FCSTD DOCUMENT  (FreeCAD 0.19R)
Label: case
License: All rights reserved
LicenseURL: http://en.wikipedia.org/wiki/All_rights_reserved
objects: Part::FeaturePython×117, Part::Cylinder×32, Part::Box×18, Part::Mirroring×3
note: 170 computed .brp shape members not serialized (recipe doc carries the construction recipe); baked Part::Feature solids carry a one-line shape summary decoded from their .brp

FEATURE [Part::Box] Box002  label="Cube002"
  AttacherType = Attacher::AttachEngine3D
  Height = 10
  Length = 5
  Placement = pos=(0,2.5,1) rot=(0,0,1;0rad)
  Width = 1
FEATURE [Part::Mirroring] Part__Mirroring  label="Cube003 (Mirror #1)"
  Base = (0,0,0)
  Normal = (1,0,0)
FEATURE [Part::Mirroring] Part__Mirroring001  label="Cube004 (Mirror #2)"
  Base = (0,0,0)
  Normal = (1,0,0)
FEATURE [Part::Mirroring] Part__Mirroring002  label="Cube005 (Mirror #3)"
  Base = (0,0,0)
  Normal = (1,0,0)
FEATURE [Part::Box] Box007  label="Cube007"
  AttacherType = Attacher::AttachEngine3D
  Height = 3
  Length = 10
  Placement = pos=(-5,0,-2) rot=(0,0,1;0rad)
  Width = 45
FEATURE [Part::Box] Box009  label="Cube009"
  AttacherType = Attacher::AttachEngine3D
  Height = 35
  Length = 44
  Placement = pos=(-2,117,1) rot=(0,0,1;0rad)
  Width = 3
FEATURE [Part::Box] Box016  label="Floor"
  AttacherType = Attacher::AttachEngine3D
  Height = 3
  Length = 50
  Placement = pos=(-5,45,-2) rot=(0,0,1;0rad)
  Width = 75
FEATURE [Part::Box] Box018  label="Cube016"
  AttacherType = Attacher::AttachEngine3D
  Height = 1
  Length = 10
  Placement = pos=(14.5,35,0) rot=(0,0,1;0rad)
  Width = 10
FEATURE [Part::Box] Box008  label="Cube008"
  AttacherType = Attacher::AttachEngine3D
  Height = 2
  Length = 30
  Placement = pos=(5,35,-1) rot=(0,0,1;0rad)
  Width = 10
FEATURE [Part::FeaturePython] Cutout005  # WARN: FeaturePython — macro-defined, semantics opaque (R4)
  Base = -> Box008
  Tolerance = 0
  Tool = -> Box018
FEATURE [Part::Box] Box  label="Cube"
  AttacherType = Attacher::AttachEngine3D
  Height = 10
  Length = 5
  Placement = pos=(0,0,1) rot=(0,0,1;0rad)
  Width = 1
FEATURE [Part::Box] Box001  label="Cube001"
  AttacherType = Attacher::AttachEngine3D
  Height = 10
  Length = 3.5
  Placement = pos=(-2e-16,0,1) rot=(0,0,1;1.5708rad)
  Width = 2
FEATURE [Part::Box] Box010  label="Cube010"
  AttacherType = Attacher::AttachEngine3D
  Height = 35
  Length = 3
  Placement = pos=(-5,0,1) rot=(0,0,1;0rad)
  Width = 120
FEATURE [Part::Box] Box020  label="Cube018"
  AttacherType = Attacher::AttachEngine3D
  Height = 3
  Length = 10
  Placement = pos=(45,-1e-14,34) rot=(0,0,1;1.5708rad)
  Width = 50
FEATURE [Part::Box] Box021  label="Cube019"
  AttacherType = Attacher::AttachEngine3D
  Height = 3
  Length = 20
  Placement = pos=(45,10,34) rot=(0,0,1;1.5708rad)
  Width = 50
FEATURE [Part::Box] Box022  label="Cube020"
  AttacherType = Attacher::AttachEngine3D
  Height = 3
  Length = 20
  Placement = pos=(40,10,31) rot=(0,0,1;1.5708rad)
  Width = 40
FEATURE [Part::Box] Box023  label="Cube021"
  AttacherType = Attacher::AttachEngine3D
  Height = 3
  Length = 90
  Placement = pos=(45,30,34) rot=(0,0,1;1.5708rad)
  Width = 50
FEATURE [Part::FeaturePython] Connect  # WARN: FeaturePython — macro-defined, semantics opaque (R4)
  Objects = -> [Part__Mirroring,Part__Mirroring002,Part__Mirroring001]
  Placement = pos=(40,0,1) rot=(0,0,1;0rad)
  Tolerance = 0
FEATURE [Part::Box] Box019  label="Cube017"
  AttacherType = Attacher::AttachEngine3D
  Height = 35
  Length = 3
  Placement = pos=(42,0,1) rot=(0,0,1;0rad)
  Width = 120
FEATURE [Part::Box] Box031  label="Cube028"
  AttacherType = Attacher::AttachEngine3D
  Height = 7
  Length = 30
  Placement = pos=(5,0,-6) rot=(0,0,1;0rad)
  Width = 7
FEATURE [Part::Box] Box032  label="Cube029"
  AttacherType = Attacher::AttachEngine3D
  Height = 4
  Length = 10
  Placement = pos=(15,0,-3) rot=(0,0,1;0rad)
  Width = 7
FEATURE [Part::Cylinder] Cylinder036  label="outer016"
  Angle = 360
  AttacherType = Attacher::AttachEngine3D
  Height = 3
  Placement = pos=(-69,17,-9) rot=(0,0,1;0rad)
  Radius = 3
FEATURE [Part::Cylinder] Cylinder038  label="M3 cutout021"
  Angle = 360
  AttacherType = Attacher::AttachEngine3D
  Height = 3
  Placement = pos=(-69,17,-9) rot=(0,0,1;0rad)
  Radius = 1.45
FEATURE [Part::FeaturePython] Cutout007  # WARN: FeaturePython — macro-defined, semantics opaque (R4)
  Base = -> Cylinder036
  Placement = pos=(64,95,7) rot=(0,0,1;0rad)
  Tolerance = 0
  Tool = -> Cylinder038
FEATURE [Part::FeaturePython] Cutout008  # WARN: FeaturePython — macro-defined, semantics opaque (R4)
  Placement = pos=(64,95,26) rot=(0,0,1;0rad)
  Tolerance = 0
FEATURE [Part::FeaturePython] Cutout011  # WARN: FeaturePython — macro-defined, semantics opaque (R4)
  Placement = pos=(114,95,7) rot=(0,0,1;0rad)
  Tolerance = 0
FEATURE [Part::Cylinder] Cylinder051  label="M3 cutout029"
  Angle = 360
  AttacherType = Attacher::AttachEngine3D
  Height = 10
  Placement = pos=(5,94,-10) rot=(0,0,1;0rad)
  Radius = 1.45
FEATURE [Part::Cylinder] Cylinder052  label="outer023"
  Angle = 360
  AttacherType = Attacher::AttachEngine3D
  Height = 10
  Placement = pos=(5,94,-10) rot=(0,0,1;0rad)
  Radius = 3
FEATURE [Part::FeaturePython] Cutout012  label="Batter holder screw 1"  # WARN: FeaturePython — macro-defined, semantics opaque (R4)
  Base = -> Cylinder052
  Placement = pos=(-1.5,3,0) rot=(0,0,1;0rad)
  Tolerance = 0
  Tool = -> Cylinder051
FEATURE [Part::Cylinder] Cylinder053  label="M3 cutout030"
  Angle = 360
  AttacherType = Attacher::AttachEngine3D
  Height = 10
  Placement = pos=(5,94,-10) rot=(0,0,1;0rad)
  Radius = 1.45
FEATURE [Part::Cylinder] Cylinder054  label="outer024"
  Angle = 360
  AttacherType = Attacher::AttachEngine3D
  Height = 10
  Placement = pos=(5,94,-10) rot=(0,0,1;0rad)
  Radius = 3
FEATURE [Part::FeaturePython] Cutout013  label="Batter holder screw 2"  # WARN: FeaturePython — macro-defined, semantics opaque (R4)
  Base = -> Cylinder054
  Placement = pos=(31.5,3,0) rot=(0,0,1;0rad)
  Tolerance = 0
  Tool = -> Cylinder053
FEATURE [Part::Cylinder] Cylinder055  label="M3 cutout031"
  Angle = 360
  AttacherType = Attacher::AttachEngine3D
  Height = 10
  Placement = pos=(5,94,-10) rot=(0,0,1;0rad)
  Radius = 1.45
FEATURE [Part::Cylinder] Cylinder056  label="outer025"
  Angle = 360
  AttacherType = Attacher::AttachEngine3D
  Height = 10
  Placement = pos=(5,94,-10) rot=(0,0,1;0rad)
  Radius = 3
FEATURE [Part::FeaturePython] Cutout014  label="Batter holder screw 3"  # WARN: FeaturePython — macro-defined, semantics opaque (R4)
  Base = -> Cylinder056
  Placement = pos=(31.5,-90,0) rot=(0,0,1;0rad)
  Tolerance = 0
  Tool = -> Cylinder055
FEATURE [Part::Cylinder] Cylinder058  label="outer026"
  Angle = 360
  AttacherType = Attacher::AttachEngine3D
  Height = 10
  Placement = pos=(5,94,-10) rot=(0,0,1;0rad)
  Radius = 3
FEATURE [Part::Cylinder] Cylinder059  label="M3 cutout033"
  Angle = 360
  AttacherType = Attacher::AttachEngine3D
  Height = 10
  Placement = pos=(5,94,-10) rot=(0,0,1;0rad)
  Radius = 1.45
FEATURE [Part::FeaturePython] Cutout018  label="Batter holder screw 004"  # WARN: FeaturePython — macro-defined, semantics opaque (R4)
  Base = -> Cylinder058
  Placement = pos=(-1.5,-90,0) rot=(0,0,1;0rad)
  Tolerance = 0
  Tool = -> Cylinder059
FEATURE [Part::Box] Box006  label="Cube006"
  AttacherType = Attacher::AttachEngine3D
  Height = 3
  Length = 10
  Placement = pos=(35,0,-2) rot=(0,0,1;0rad)
  Width = 45
FEATURE [Part::Cylinder] Cylinder060  label="M3 cutout034"
  Angle = 360
  AttacherType = Attacher::AttachEngine3D
  Height = 12
  Placement = pos=(-5,112,-2) rot=(0,0,1;0rad)
  Radius = 1.45
FEATURE [Part::FeaturePython] Cutout019  # WARN: FeaturePython — macro-defined, semantics opaque (R4)
  Base = -> Box016
  Tolerance = 0
  Tool = -> Cylinder060
FEATURE [Part::FeaturePython] Cutout020  # WARN: FeaturePython — macro-defined, semantics opaque (R4)
  Base = -> Box010
  Tolerance = 0
  Tool = -> Cylinder060
FEATURE [Part::Cylinder] Cylinder061  label="M3 cutout035"
  Angle = 360
  AttacherType = Attacher::AttachEngine3D
  Height = 12
  Placement = pos=(45,112,-2) rot=(0,0,1;0rad)
  Radius = 1.45
FEATURE [Part::FeaturePython] Cutout021  # WARN: FeaturePython — macro-defined, semantics opaque (R4)
  Base = -> Box019
  Tolerance = 0
  Tool = -> Cylinder061
FEATURE [Part::FeaturePython] Cutout022  # WARN: FeaturePython — macro-defined, semantics opaque (R4)
  Base = -> Cutout019
  Tolerance = 0
  Tool = -> Cylinder061
FEATURE [Part::Cylinder] Cylinder062  label="M3 cutout036"
  Angle = 360
  AttacherType = Attacher::AttachEngine3D
  Height = 1
  Placement = pos=(-5,112,10) rot=(0,0,1;0rad)
  Radius = 1.45
FEATURE [Part::Cylinder] Cylinder064  label="outer027"
  Angle = 360
  AttacherType = Attacher::AttachEngine3D
  Height = 3
  Placement = pos=(-69,17,-9) rot=(0,0,1;0rad)
  Radius = 3
FEATURE [Part::Cylinder] Cylinder065  label="M3 cutout038"
  Angle = 360
  AttacherType = Attacher::AttachEngine3D
  Height = 3
  Placement = pos=(-69,17,-9) rot=(0,0,1;0rad)
  Radius = 1.45
FEATURE [Part::FeaturePython] Cutout024  # WARN: FeaturePython — macro-defined, semantics opaque (R4)
  Base = -> Cylinder064
  Placement = pos=(64,-5,7) rot=(0,0,1;0rad)
  Tolerance = 0
  Tool = -> Cylinder065
FEATURE [Part::Cylinder] Cylinder067  label="M3 cutout039"
  Angle = 360
  AttacherType = Attacher::AttachEngine3D
  Height = 12
  Placement = pos=(-5,12,-2) rot=(0,0,1;0rad)
  Radius = 1.45
FEATURE [Part::FeaturePython] Cutout025  # WARN: FeaturePython — macro-defined, semantics opaque (R4)
  Base = -> Box007
  Tolerance = 0
  Tool = -> Cylinder067
FEATURE [Part::FeaturePython] Cutout026  # WARN: FeaturePython — macro-defined, semantics opaque (R4)
  Base = -> Cutout020
  Tolerance = 0
  Tool = -> Cylinder067
FEATURE [Part::Cylinder] Cylinder073  label="M3 cutout043"
  Angle = 360
  AttacherType = Attacher::AttachEngine3D
  Height = 12
  Placement = pos=(45,12,-2) rot=(0,0,1;0rad)
  Radius = 1.45
FEATURE [Part::FeaturePython] Cutout029  # WARN: FeaturePython — macro-defined, semantics opaque (R4)
  Base = -> Cutout021
  Tolerance = 0
  Tool = -> Cylinder073
FEATURE [Part::FeaturePython] Cutout030  # WARN: FeaturePython — macro-defined, semantics opaque (R4)
  Base = -> Box006
  Tolerance = 0
  Tool = -> Cylinder073
FEATURE [Part::FeaturePython] Cutout  # WARN: FeaturePython — macro-defined, semantics opaque (R4)
  Base = -> Box031
  Tolerance = 0
  Tool = -> Box032
FEATURE [Part::FeaturePython] Cutout015  # WARN: FeaturePython — macro-defined, semantics opaque (R4)
  Base = -> Cutout
  Tolerance = 0
  Tool = -> Cylinder055
FEATURE [Part::Box] Box033  label="Cube030"
  AttacherType = Attacher::AttachEngine3D
  Height = 4
  Length = 10
  Placement = pos=(-5,0,-6) rot=(0,0,1;0rad)
  Width = 7
FEATURE [Part::Cylinder] Cylinder074  label="M3 cutout044"
  Angle = 360
  AttacherType = Attacher::AttachEngine3D
  Height = 10
  Placement = pos=(3.5,4,-10) rot=(0,0,1;0rad)
  Radius = 1.45
FEATURE [Part::FeaturePython] Cutout031  # WARN: FeaturePython — macro-defined, semantics opaque (R4)
  Base = -> Box033
  Tolerance = 0
  Tool = -> Cylinder074
FEATURE [Part::FeaturePython] Cutout032  # WARN: FeaturePython — macro-defined, semantics opaque (R4)
  Base = -> Box033
  Placement = pos=(40,1e-15,-8) rot=(0,1,0;3.14159rad)
  Tolerance = 0
  Tool = -> Cylinder074
FEATURE [Part::Cylinder] Cylinder076  label="M3 cutout046"
  Angle = 360
  AttacherType = Attacher::AttachEngine3D
  Height = 1
  Placement = pos=(44.9494,112,9.86308) rot=(0,0,1;0rad)
  Radius = 1.45
FEATURE [Part::Cylinder] Cylinder077  label="M3 cutout047"
  Angle = 360
  AttacherType = Attacher::AttachEngine3D
  Height = 1
  Placement = pos=(44.9494,12,9.86308) rot=(0,0,1;0rad)
  Radius = 1.45
FEATURE [Part::FeaturePython] Connect006  # WARN: FeaturePython — macro-defined, semantics opaque (R4)
  Objects = -> [Cutout008,Cylinder062]
  Placement = pos=(0,-100,0) rot=(0,0,1;0rad)
  Tolerance = 0
FEATURE [Part::FeaturePython] Connect007  # WARN: FeaturePython — macro-defined, semantics opaque (R4)
  Objects = -> [Cutout008,Cylinder062]
  Placement = pos=(50,0,0) rot=(0,0,1;0rad)
  Tolerance = 0
FEATURE [Part::FeaturePython] Connect008  # WARN: FeaturePython — macro-defined, semantics opaque (R4)
  Objects = -> [Cutout008,Cylinder062]
  Placement = pos=(50,-100,0) rot=(0,0,1;0rad)
  Tolerance = 0
FEATURE [Part::FeaturePython] Connect009  # WARN: FeaturePython — macro-defined, semantics opaque (R4)
  Objects = -> [Cutout008,Cylinder062]
  Placement = pos=(50,124,37) rot=(1,0,0;3.14159rad)
  Tolerance = 0
FEATURE [Part::Cylinder] Cylinder078  label="M3 cutout048"
  Angle = 360
  AttacherType = Attacher::AttachEngine3D
  Height = 10
  Placement = pos=(45,12,26) rot=(0,0,1;0rad)
  Radius = 1.45
FEATURE [Part::FeaturePython] Cutout033  # WARN: FeaturePython — macro-defined, semantics opaque (R4)
  Base = -> Cutout029
  Tolerance = 0
  Tool = -> Cylinder078
FEATURE [Part::FeaturePython] Connect011  # WARN: FeaturePython — macro-defined, semantics opaque (R4)
  Objects = -> [Cutout008,Cylinder062]
  Placement = pos=(50,224,37) rot=(1,0,0;3.14159rad)
  Tolerance = 0
FEATURE [Part::Cylinder] Cylinder079  label="M3 cutout049"
  Angle = 360
  AttacherType = Attacher::AttachEngine3D
  Height = 10
  Placement = pos=(45,112,26) rot=(0,0,1;0rad)
  Radius = 1.45
FEATURE [Part::FeaturePython] Cutout034  # WARN: FeaturePython — macro-defined, semantics opaque (R4)
  Base = -> Cutout033
  Tolerance = 0
  Tool = -> Cylinder079
FEATURE [Part::FeaturePython] Cutout035  # WARN: FeaturePython — macro-defined, semantics opaque (R4)
  Placement = pos=(64,95,26) rot=(0,0,1;0rad)
  Tolerance = 0
FEATURE [Part::Cylinder] Cylinder080  label="M3 cutout050"
  Angle = 360
  AttacherType = Attacher::AttachEngine3D
  Height = 1
  Placement = pos=(-5,112,10) rot=(0,0,1;0rad)
  Radius = 1.45
FEATURE [Part::Cylinder] Cylinder081  label="M3 cutout051"
  Angle = 360
  AttacherType = Attacher::AttachEngine3D
  Height = 10
  Placement = pos=(-5,112,26) rot=(0,0,1;0rad)
  Radius = 1.45
FEATURE [Part::FeaturePython] Cutout036  # WARN: FeaturePython — macro-defined, semantics opaque (R4)
  Base = -> Cutout026
  Tolerance = 0
  Tool = -> Cylinder081
FEATURE [Part::FeaturePython] Connect013  # WARN: FeaturePython — macro-defined, semantics opaque (R4)
  Objects = -> [Cutout008,Cylinder062]
  Placement = pos=(0,124,37) rot=(1,0,0;3.14159rad)
  Tolerance = 0
FEATURE [Part::Cylinder] Cylinder082  label="M3 cutout052"
  Angle = 360
  AttacherType = Attacher::AttachEngine3D
  Height = 10
  Placement = pos=(-5,12,26) rot=(0,0,1;0rad)
  Radius = 1.45
FEATURE [Part::FeaturePython] Cutout037  # WARN: FeaturePython — macro-defined, semantics opaque (R4)
  Base = -> Cutout036
  Tolerance = 0
  Tool = -> Cylinder082
FEATURE [Part::FeaturePython] Connect012  # WARN: FeaturePython — macro-defined, semantics opaque (R4)
  Objects = -> [Cutout035,Cylinder080]
  Placement = pos=(0,224,37) rot=(1,0,0;3.14159rad)
  Tolerance = 0
FEATURE [Part::FeaturePython] Connect005  # WARN: FeaturePython — macro-defined, semantics opaque (R4)
  Objects = -> [Cutout008,Cylinder062]
  Tolerance = 0
FEATURE [Part::FeaturePython] Cutout038  # WARN: FeaturePython — macro-defined, semantics opaque (R4)
  Base = -> Cylinder064
  Placement = pos=(64,-5,43) rot=(0,0,1;0rad)
  Tolerance = 0
  Tool = -> Cylinder065
FEATURE [Part::Cylinder] Cylinder083  label="M3 cutout053"
  Angle = 360
  AttacherType = Attacher::AttachEngine3D
  Height = 3
  Placement = pos=(-5,12,34) rot=(0,0,1;0rad)
  Radius = 1.45
FEATURE [Part::FeaturePython] Cutout039  # WARN: FeaturePython — macro-defined, semantics opaque (R4)
  Base = -> Box021
  Tolerance = 0
  Tool = -> Cylinder083
FEATURE [Part::FeaturePython] Cutout040  # WARN: FeaturePython — macro-defined, semantics opaque (R4)
  Base = -> Cylinder064
  Placement = pos=(114,-5,43) rot=(0,0,1;0rad)
  Tolerance = 0
  Tool = -> Cylinder065
FEATURE [Part::Cylinder] Cylinder084  label="M3 cutout054"
  Angle = 360
  AttacherType = Attacher::AttachEngine3D
  Height = 3
  Placement = pos=(45,12,34) rot=(0,0,1;0rad)
  Radius = 1.45
FEATURE [Part::FeaturePython] Cutout041  # WARN: FeaturePython — macro-defined, semantics opaque (R4)
  Base = -> Cutout039
  Tolerance = 0
  Tool = -> Cylinder084
FEATURE [Part::FeaturePython] Cutout042  # WARN: FeaturePython — macro-defined, semantics opaque (R4)
  Base = -> Cylinder064
  Placement = pos=(114,95,43) rot=(0,0,1;0rad)
  Tolerance = 0
  Tool = -> Cylinder065
FEATURE [Part::Cylinder] Cylinder085  label="M3 cutout055"
  Angle = 360
  AttacherType = Attacher::AttachEngine3D
  Height = 3
  Placement = pos=(45,112,34) rot=(0,0,1;0rad)
  Radius = 1.45
FEATURE [Part::FeaturePython] Cutout043  # WARN: FeaturePython — macro-defined, semantics opaque (R4)
  Base = -> Box023
  Tolerance = 0
  Tool = -> Cylinder085
FEATURE [Part::FeaturePython] Cutout044  # WARN: FeaturePython — macro-defined, semantics opaque (R4)
  Base = -> Cylinder064
  Placement = pos=(64,95,43) rot=(0,0,1;0rad)
  Tolerance = 0
  Tool = -> Cylinder065
FEATURE [Part::Cylinder] Cylinder086  label="M3 cutout056"
  Angle = 360
  AttacherType = Attacher::AttachEngine3D
  Height = 3
  Placement = pos=(-5,112,34) rot=(0,0,1;0rad)
  Radius = 1.45
FEATURE [Part::FeaturePython] Cutout045  # WARN: FeaturePython — macro-defined, semantics opaque (R4)
  Base = -> Cutout043
  Tolerance = 0
  Tool = -> Cylinder086
FEATURE [Part::FeaturePython] ScrewTap001  label="M3x10.0-ScrewTap006"  # Fasteners workbench fastener (typed FeaturePython)
  Placement = pos=(36.5,4,-10) rot=(0,0,1;0rad)
  baseObject = -> Cutout014 [Edge5]
  diameter = 4
  diameterCustom = 6
  invert = false
  length = 10
  matchOuter = false
  offset = 0
  pitchCustom = 1
  thread = true
FEATURE [Part::FeaturePython] ScrewTap002  label="M3x10.0-ScrewTap"  # Fasteners workbench fastener (typed FeaturePython)
  Placement = pos=(3.5,4,-10) rot=(0,0,1;0rad)
  baseObject = -> Cutout018 [Edge5]
  diameter = 4
  diameterCustom = 6
  invert = false
  length = 10
  matchOuter = false
  offset = 0
  pitchCustom = 1
  thread = true
FEATURE [Part::FeaturePython] ScrewTap003  label="M3x12.0-ScrewTap004"  # Fasteners workbench fastener (typed FeaturePython)
  Placement = pos=(-5,12,10.5) rot=(0,0,1;0rad)
  diameter = 4
  diameterCustom = 6
  invert = false
  length = 12
  matchOuter = false
  offset = 0
  pitchCustom = 1
  thread = true
FEATURE [Part::FeaturePython] ScrewTap006  label="M3x12.0-ScrewTap"  # Fasteners workbench fastener (typed FeaturePython)
  Placement = pos=(45,112,10.5) rot=(0,0,1;0rad)
  diameter = 4
  diameterCustom = 6
  invert = false
  length = 12
  matchOuter = false
  offset = 0
  pitchCustom = 1
  thread = true
FEATURE [Part::FeaturePython] ScrewTap007  label="M3x12.0-ScrewTap005"  # Fasteners workbench fastener (typed FeaturePython)
  Placement = pos=(-5,112,10.5) rot=(0,0,1;0rad)
  diameter = 4
  diameterCustom = 6
  invert = false
  length = 12
  matchOuter = false
  offset = 0
  pitchCustom = 1
  thread = true
FEATURE [Part::FeaturePython] Cutout046  # WARN: FeaturePython — macro-defined, semantics opaque (R4)
  Base = -> Cutout011
  Tolerance = 0
  Tool = -> ScrewTap006
FEATURE [Part::FeaturePython] Cutout047  # WARN: FeaturePython — macro-defined, semantics opaque (R4)
  Base = -> Connect007
  Tolerance = 0
  Tool = -> ScrewTap006
FEATURE [Part::FeaturePython] Cutout049  # WARN: FeaturePython — macro-defined, semantics opaque (R4)
  Base = -> Cutout022
  Tolerance = 0
FEATURE [Part::FeaturePython] Cutout051  # WARN: FeaturePython — macro-defined, semantics opaque (R4)
  Base = -> Cutout049
  Tolerance = 0
FEATURE [Part::FeaturePython] Cutout052  # WARN: FeaturePython — macro-defined, semantics opaque (R4)
  Base = -> Cutout007
  Tolerance = 0
  Tool = -> ScrewTap007
FEATURE [Part::FeaturePython] Cutout053  # WARN: FeaturePython — macro-defined, semantics opaque (R4)
  Base = -> Connect005
  Tolerance = 0
  Tool = -> ScrewTap007
FEATURE [Part::FeaturePython] Cutout056  # WARN: FeaturePython — macro-defined, semantics opaque (R4)
  Base = -> Cutout032
  Tolerance = 0
  Tool = -> ScrewTap001
FEATURE [Part::FeaturePython] Cutout057  # WARN: FeaturePython — macro-defined, semantics opaque (R4)
  Base = -> Cutout014
  Tolerance = 0
  Tool = -> ScrewTap001
FEATURE [Part::FeaturePython] Cutout058  # WARN: FeaturePython — macro-defined, semantics opaque (R4)
  Base = -> Cutout015
  Tolerance = 0
FEATURE [Part::FeaturePython] Cutout059  # WARN: FeaturePython — macro-defined, semantics opaque (R4)
  Base = -> Cutout030
  Tolerance = 0
  Tool = -> ScrewTap001
FEATURE [Part::FeaturePython] Cutout060  # WARN: FeaturePython — macro-defined, semantics opaque (R4)
  Base = -> Cutout058
  Tolerance = 0
  Tool = -> ScrewTap002
FEATURE [Part::FeaturePython] Cutout062  # WARN: FeaturePython — macro-defined, semantics opaque (R4)
  Base = -> Cutout031
  Tolerance = 0
  Tool = -> ScrewTap002
FEATURE [Part::FeaturePython] Cutout063  # WARN: FeaturePython — macro-defined, semantics opaque (R4)
  Base = -> Cutout025
  Tolerance = 0
  Tool = -> ScrewTap002
FEATURE [Part::FeaturePython] Cutout064  # WARN: FeaturePython — macro-defined, semantics opaque (R4)
  Base = -> Cutout024
  Tolerance = 0
  Tool = -> ScrewTap003
FEATURE [Part::FeaturePython] Cutout065  # WARN: FeaturePython — macro-defined, semantics opaque (R4)
  Base = -> Connect006
  Tolerance = 0
  Tool = -> ScrewTap003
FEATURE [Part::FeaturePython] Connect016  label="lid"  # WARN: FeaturePython — macro-defined, semantics opaque (R4)
  Objects = -> [Box020,Box022,Cutout040,Cutout041,Cutout045,Cutout044,Cutout042,Cutout038]
  Placement = pos=(0,0,2) rot=(0,0,1;0rad)
  Tolerance = 0
FEATURE [Part::FeaturePython] ScrewTap008  label="M3x12.0-ScrewTap019"  # Fasteners workbench fastener (typed FeaturePython)
  Placement = pos=(45,12,36) rot=(1,0,0;3.14159rad)
  baseObject = -> Connect009 [Edge5]
  diameter = 4
  diameterCustom = 6
  invert = false
  length = 12
  matchOuter = false
  offset = 0
  pitchCustom = 1
  thread = true
FEATURE [Part::FeaturePython] ScrewTap010  label="M3x12.0-ScrewTap012"  # Fasteners workbench fastener (typed FeaturePython)
  Placement = pos=(-5,12,39) rot=(0,0,1;0rad)
  baseObject = -> Connect016 [Edge59]
  diameter = 4
  diameterCustom = 6
  invert = false
  length = 12
  matchOuter = false
  offset = 0
  pitchCustom = 1
  thread = true
FEATURE [Part::FeaturePython] ScrewTap011  label="(M3.5)x12.0-ScrewTap"  # Fasteners workbench fastener (typed FeaturePython)
  Placement = pos=(-5,112,39) rot=(0,0,1;0rad)
  baseObject = -> Connect016 [Edge37]
  diameter = 5
  diameterCustom = 12
  invert = false
  length = 12
  matchOuter = false
  offset = 0
  pitchCustom = 1
  thread = true
FEATURE [Part::Cylinder] Cylinder087  label="M3 cutout057"
  Angle = 360
  AttacherType = Attacher::AttachEngine3D
  Height = 1
  Placement = pos=(-5,112,10) rot=(0,0,1;0rad)
  Radius = 1.45
FEATURE [Part::FeaturePython] Cutout067  # WARN: FeaturePython — macro-defined, semantics opaque (R4)
  Placement = pos=(64,95,26) rot=(0,0,1;0rad)
  Tolerance = 0
FEATURE [Part::FeaturePython] Connect018  # WARN: FeaturePython — macro-defined, semantics opaque (R4)
  Objects = -> [Cutout067,Cylinder087]
  Placement = pos=(0,-100,0) rot=(0,0,1;0rad)
  Tolerance = 0
FEATURE [Part::FeaturePython] Cutout066  # WARN: FeaturePython — macro-defined, semantics opaque (R4)
  Base = -> Connect018
  Placement = pos=(50,0,0) rot=(0,0,1;0rad)
  Tolerance = 0
FEATURE [Part::FeaturePython] Cutout068  # WARN: FeaturePython — macro-defined, semantics opaque (R4)
  Base = -> Connect016
  Tolerance = 0
  Tool = -> ScrewTap008
FEATURE [Part::FeaturePython] Cutout070  # WARN: FeaturePython — macro-defined, semantics opaque (R4)
  Base = -> Cutout068
  Tolerance = 0
  Tool = -> ScrewTap010
FEATURE [Part::FeaturePython] Cutout071  # WARN: FeaturePython — macro-defined, semantics opaque (R4)
  Base = -> Connect013
  Tolerance = 0
  Tool = -> ScrewTap010
FEATURE [Part::FeaturePython] ScrewTap013  label="M3x12.0-ScrewTap020"  # Fasteners workbench fastener (typed FeaturePython)
  Placement = pos=(45,112,39) rot=(0,0,1;0rad)
  baseObject = -> Cutout070 [Edge160]
  diameter = 4
  diameterCustom = 6
  invert = false
  length = 12
  matchOuter = false
  offset = 0
  pitchCustom = 1
  thread = true
FEATURE [Part::FeaturePython] Cutout072  # WARN: FeaturePython — macro-defined, semantics opaque (R4)
  Base = -> Cutout070
  Tolerance = 0
  Tool = -> ScrewTap013
FEATURE [Part::FeaturePython] Cutout074  # WARN: FeaturePython — macro-defined, semantics opaque (R4)
  Base = -> Cutout072
  Tolerance = 0
  Tool = -> ScrewTap011
FEATURE [Part::FeaturePython] Cutout075  # WARN: FeaturePython — macro-defined, semantics opaque (R4)
  Base = -> Connect012
  Tolerance = 0
  Tool = -> ScrewTap011
FEATURE [Part::FeaturePython] Cutout076  # WARN: FeaturePython — macro-defined, semantics opaque (R4)
  Base = -> Cutout074
  Tolerance = 0
  Tool = -> ScrewTap013
FEATURE [Part::FeaturePython] Cutout077  # WARN: FeaturePython — macro-defined, semantics opaque (R4)
  Base = -> Cutout034
  Tolerance = 0
  Tool = -> ScrewTap013
FEATURE [Part::FeaturePython] Tube  # WARN: FeaturePython — macro-defined, semantics opaque (R4)
  AttacherType = Attacher::AttachEngine3D
  Height = 3
  InnerRadius = 0.5
  OuterRadius = 1
  Placement = pos=(16.5,117,4) rot=(0,0.707107,0.707107;3.14159rad)
FEATURE [Part::FeaturePython] Tube001  # WARN: FeaturePython — macro-defined, semantics opaque (R4)
  AttacherType = Attacher::AttachEngine3D
  Height = 3
  InnerRadius = 0.5
  OuterRadius = 1
  Placement = pos=(19,117,4) rot=(-1,0,0;1.5708rad)
FEATURE [Part::FeaturePython] Tube002  # WARN: FeaturePython — macro-defined, semantics opaque (R4)
  AttacherType = Attacher::AttachEngine3D
  Height = 3
  InnerRadius = 0.5
  OuterRadius = 1
  Placement = pos=(21.5,117,4) rot=(-1,0,0;1.5708rad)
FEATURE [Part::FeaturePython] Tube003  # WARN: FeaturePython — macro-defined, semantics opaque (R4)
  AttacherType = Attacher::AttachEngine3D
  Height = 3
  InnerRadius = 0.5
  OuterRadius = 1
  Placement = pos=(24,117,4) rot=(-1,0,0;1.5708rad)
FEATURE [Part::FeaturePython] Cutout078  # WARN: FeaturePython — macro-defined, semantics opaque (R4)
  Base = -> Box009
  Tolerance = 0
  Tool = -> Tube
FEATURE [Part::FeaturePython] Cutout079  # WARN: FeaturePython — macro-defined, semantics opaque (R4)
  Base = -> Cutout078
  Tolerance = 0
  Tool = -> Tube001
FEATURE [Part::FeaturePython] Cutout080  # WARN: FeaturePython — macro-defined, semantics opaque (R4)
  Base = -> Cutout079
  Tolerance = 0
  Tool = -> Tube002
FEATURE [Part::FeaturePython] Cutout081  # WARN: FeaturePython — macro-defined, semantics opaque (R4)
  Base = -> Cutout080
  Tolerance = 0
  Tool = -> Tube003
FEATURE [Part::FeaturePython] Cutout082  # WARN: FeaturePython — macro-defined, semantics opaque (R4)
  Base = -> Connect009
  Tolerance = 0
  Tool = -> ScrewTap008
FEATURE [Part::FeaturePython] Cutout084  # WARN: FeaturePython — macro-defined, semantics opaque (R4)
  Base = -> Connect011
  Tolerance = 0
  Tool = -> ScrewTap013
FEATURE [Part::Cylinder] Cylinder088  label="M3 cutout058"
  Angle = 360
  AttacherType = Attacher::AttachEngine3D
  Height = 3
  Placement = pos=(-69,17,-9) rot=(0,0,1;0rad)
  Radius = 1.45
FEATURE [Part::FeaturePython] ScrewTap016  label="M3x12.0-ScrewTap018"  # Fasteners workbench fastener (typed FeaturePython)
  Placement = pos=(-5,12,10.5) rot=(0,0,1;0rad)
  diameter = 4
  diameterCustom = 6
  invert = false
  length = 12
  matchOuter = false
  offset = 0
  pitchCustom = 1
  thread = true
FEATURE [Part::Cylinder] Cylinder089  label="outer028"
  Angle = 360
  AttacherType = Attacher::AttachEngine3D
  Height = 3
  Placement = pos=(-69,17,-9) rot=(0,0,1;0rad)
  Radius = 3
FEATURE [Part::FeaturePython] Cutout086  # WARN: FeaturePython — macro-defined, semantics opaque (R4)
  Base = -> Cylinder089
  Placement = pos=(64,-5,7) rot=(0,0,1;0rad)
  Tolerance = 0
  Tool = -> Cylinder088
FEATURE [Part::FeaturePython] Cutout085  # WARN: FeaturePython — macro-defined, semantics opaque (R4)
  Base = -> Cutout086
  Placement = pos=(50,0,0) rot=(0,0,1;0rad)
  Tolerance = 0
  Tool = -> ScrewTap016
FEATURE [Part::FeaturePython] Cutout087  # WARN: FeaturePython — macro-defined, semantics opaque (R4)
  Base = -> Cutout018
  Tolerance = 0
  Tool = -> ScrewTap002
FEATURE [Part::FeaturePython] ScrewTap  label="M3x10.0-ScrewTap007"  # Fasteners workbench fastener (typed FeaturePython)
  Placement = pos=(36.5,97,-10) rot=(0,0,1;0rad)
  baseObject = -> Cutout013 [Edge5]
  diameter = 4
  diameterCustom = 6
  invert = false
  length = 10
  matchOuter = false
  offset = 0
  pitchCustom = 1
  thread = true
FEATURE [Part::FeaturePython] Cutout088  # WARN: FeaturePython — macro-defined, semantics opaque (R4)
  Base = -> Cutout013
  Tolerance = 0
  Tool = -> ScrewTap
FEATURE [Part::FeaturePython] Cutout089  # WARN: FeaturePython — macro-defined, semantics opaque (R4)
  Base = -> Cutout051
  Tolerance = 0
  Tool = -> ScrewTap
FEATURE [Part::FeaturePython] ScrewTap017  label="M3x10.0-ScrewTap008"  # Fasteners workbench fastener (typed FeaturePython)
  Placement = pos=(3.5,97,-10) rot=(0,0,1;0rad)
  baseObject = -> Cutout012 [Edge5]
  diameter = 4
  diameterCustom = 6
  invert = false
  length = 10
  matchOuter = false
  offset = 0
  pitchCustom = 1
  thread = true
FEATURE [Part::FeaturePython] Cutout090  # WARN: FeaturePython — macro-defined, semantics opaque (R4)
  Base = -> Cutout012
  Tolerance = 0
  Tool = -> ScrewTap017
FEATURE [Part::FeaturePython] Cutout091  # WARN: FeaturePython — macro-defined, semantics opaque (R4)
  Base = -> Cutout089
  Tolerance = 0
  Tool = -> ScrewTap017
FEATURE [Part::FeaturePython] ScrewTap018  label="M3x10.0-ScrewTap022"  # Fasteners workbench fastener (typed FeaturePython)
  Placement = pos=(36.5,4,-10) rot=(0,0,1;0rad)
  baseObject = -> Cutout057 [Edge5]
  diameter = 4
  diameterCustom = 6
  invert = false
  length = 10
  matchOuter = false
  offset = 0
  pitchCustom = 1
  thread = true
FEATURE [Part::FeaturePython] Cutout092  # WARN: FeaturePython — macro-defined, semantics opaque (R4)
  Base = -> Cutout057
  Tolerance = 0
  Tool = -> ScrewTap018
FEATURE [Part::FeaturePython] ScrewTap019  label="M3x10.0-ScrewTap023"  # Fasteners workbench fastener (typed FeaturePython)
  Placement = pos=(3.5,4,-10) rot=(0,0,1;0rad)
  baseObject = -> Cutout087 [Edge5]
  diameter = 4
  diameterCustom = 6
  invert = false
  length = 10
  matchOuter = false
  offset = 0
  pitchCustom = 1
  thread = true
FEATURE [Part::FeaturePython] ScrewTap020  label="M3x10.0-ScrewTap024"  # Fasteners workbench fastener (typed FeaturePython)
  Placement = pos=(3.5,97,-10) rot=(0,0,1;0rad)
  baseObject = -> Cutout090 [Edge5]
  diameter = 4
  diameterCustom = 6
  invert = false
  length = 10
  matchOuter = false
  offset = 0
  pitchCustom = 1
  thread = true
FEATURE [Part::FeaturePython] ScrewTap021  label="M3x10.0-ScrewTap025"  # Fasteners workbench fastener (typed FeaturePython)
  Placement = pos=(36.5,97,-10) rot=(0,0,1;0rad)
  baseObject = -> Cutout088 [Edge5]
  diameter = 4
  diameterCustom = 6
  invert = false
  length = 10
  matchOuter = false
  offset = 0
  pitchCustom = 1
  thread = true
FEATURE [Part::FeaturePython] Cutout093  # WARN: FeaturePython — macro-defined, semantics opaque (R4)
  Base = -> Cutout088
  Tolerance = 0
  Tool = -> ScrewTap021
FEATURE [Part::FeaturePython] Cutout094  # WARN: FeaturePython — macro-defined, semantics opaque (R4)
  Base = -> Cutout092
  Tolerance = 0
  Tool = -> ScrewTap018
FEATURE [Part::FeaturePython] Cutout095  # WARN: FeaturePython — macro-defined, semantics opaque (R4)
  Base = -> Cutout087
  Tolerance = 0
  Tool = -> ScrewTap019
FEATURE [Part::FeaturePython] Cutout096  # WARN: FeaturePython — macro-defined, semantics opaque (R4)
  Base = -> Cutout090
  Tolerance = 0
  Tool = -> ScrewTap020
FEATURE [Part::FeaturePython] Cutout097  # WARN: FeaturePython — macro-defined, semantics opaque (R4)
  Base = -> Cutout063
  Tolerance = 0
  Tool = -> ScrewTap019
FEATURE [Part::FeaturePython] Cutout098  # WARN: FeaturePython — macro-defined, semantics opaque (R4)
  Base = -> Cutout059
  Tolerance = 0
  Tool = -> ScrewTap018
FEATURE [Part::FeaturePython] Cutout099  # WARN: FeaturePython — macro-defined, semantics opaque (R4)
  Base = -> Cutout091
  Tolerance = 0
  Tool = -> ScrewTap020
FEATURE [Part::FeaturePython] Cutout100  # WARN: FeaturePython — macro-defined, semantics opaque (R4)
  Base = -> Cutout099
  Tolerance = 0
  Tool = -> ScrewTap019
FEATURE [Part::FeaturePython] Connect020  # WARN: FeaturePython — macro-defined, semantics opaque (R4)
  Objects = -> [Cutout037,Cutout065,Cutout071,Cutout075,Cutout053,Cutout081,Cutout077,Cutout084,Cutout047,Cutout082,Connect008,Cutout066,Box,Box002,Box001,Connect,Cylinder076,Cylinder077]
  Tolerance = 0
FEATURE [Part::FeaturePython] Connect021  # WARN: FeaturePython — macro-defined, semantics opaque (R4)
  Objects = -> [Cutout100,Cutout005,Cutout046,Cutout052,Cutout056,Cutout060,Cutout062,Cutout064,Cutout085,Cutout093,Cutout094,Cutout095,Cutout096,Cutout097,Cutout098,Cutout063]
  Tolerance = 0
FEATURE [Part::FeaturePython] ScrewTap022  label="M3x12.0-ScrewTap021"  # Fasteners workbench fastener (typed FeaturePython)
  Placement = pos=(45,12,39) rot=(0,0,1;0rad)
  baseObject = -> Cutout076 [Edge3]
  diameter = 4
  diameterCustom = 6
  invert = false
  length = 12
  matchOuter = false
  offset = 0
  pitchCustom = 1
  thread = true
FEATURE [Part::FeaturePython] Cutout101  # WARN: FeaturePython — macro-defined, semantics opaque (R4)
  Base = -> Connect020
  Tolerance = 0
  Tool = -> ScrewTap022
FEATURE [Part::FeaturePython] Cutout102  # WARN: FeaturePython — macro-defined, semantics opaque (R4)
  Base = -> Cutout076
  Tolerance = 0
  Tool = -> ScrewTap013
